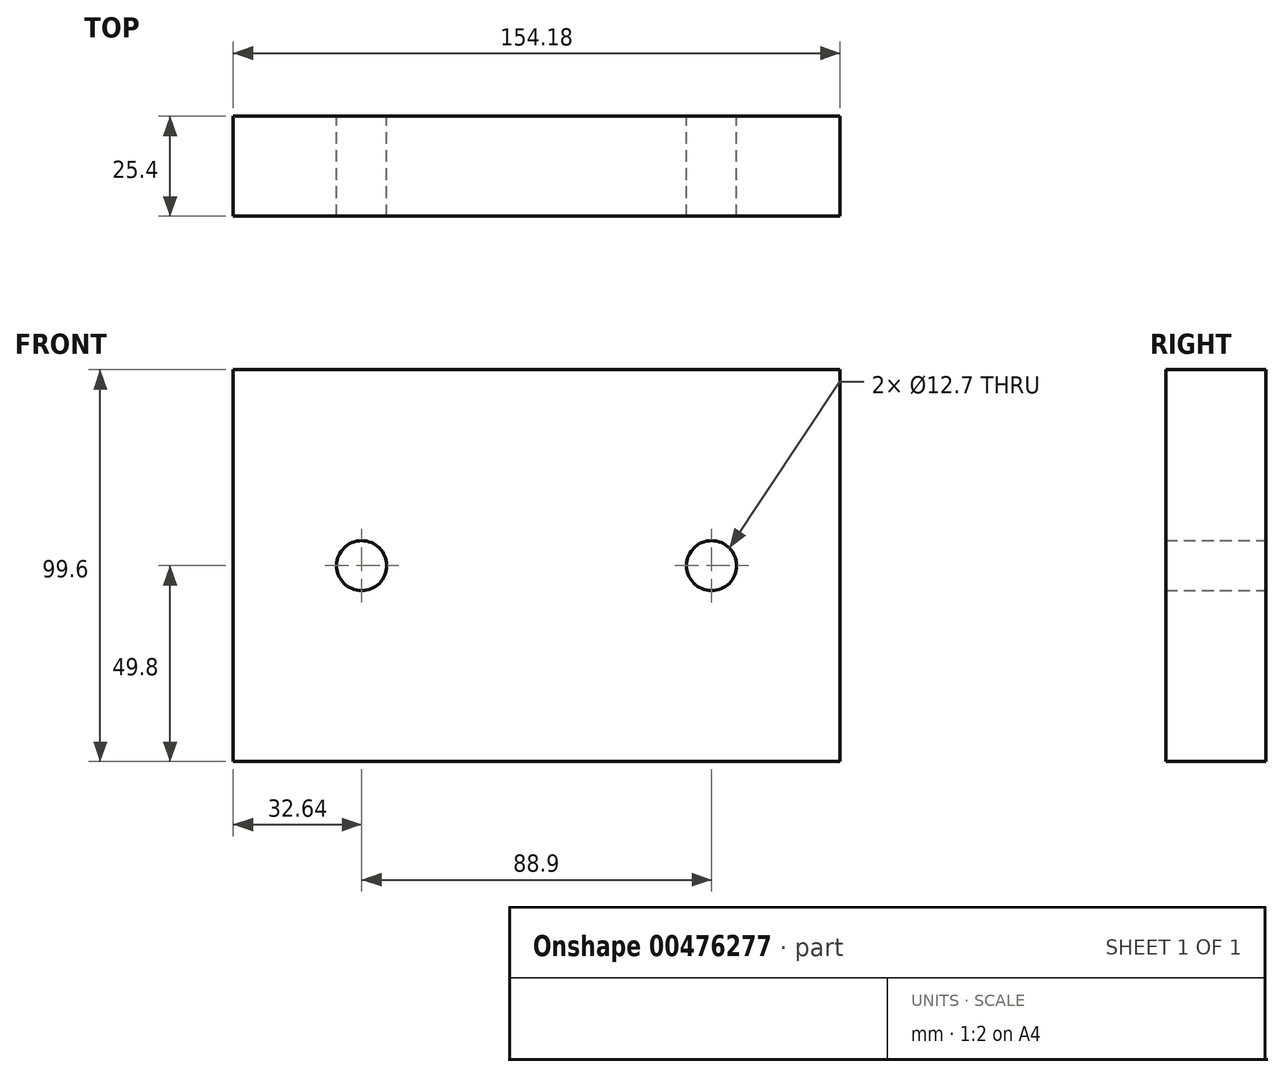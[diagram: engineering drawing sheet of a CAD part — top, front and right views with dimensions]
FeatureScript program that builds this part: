
annotation { "Feature Type Name" : "Feature", "Feature Type Description" : "" }
export const myFeature = defineFeature(function(context is Context, id is Id, definition is map)
    precondition{}
    {
        {
            var Q0;
            Q0=qCreatedBy(makeId("Front.planeOp"),FACE);
            var sketch = newSketch(context, id + "F0", { "sketchPlane" : qUnion([Q0])});
            skLineSegment(sketch, "E0.bottom", {"start": v(-77.09, 49.8) * mm, "end": v(77.09, 49.8) * mm});
            skLineSegment(sketch, "E0.top", {"start": v(-77.09, -49.8) * mm, "end": v(77.09, -49.8) * mm});
            skLineSegment(sketch, "E0.left", {"start": v(-77.09, 49.8) * mm, "end": v(-77.09, -49.8) * mm});
            skLineSegment(sketch, "E0.right", {"start": v(77.09, 49.8) * mm, "end": v(77.09, -49.8) * mm});
            skPoint(sketch, "E0.middle", {"position": v(0, 0) * mm});
            skCircle(sketch, "E1", {"center": v(-44.45, 0) * mm, "radius": 6.35 * mm});
            skCircle(sketch, "E2", {"center": v(44.45, 0) * mm, "radius": 6.35 * mm});
            skCircle(sketch, "E3", {"center": v(-44.45, 0) * mm, "radius": 50.8 * mm, "construction": true});
            skCircle(sketch, "E4", {"center": v(-44.45, 0) * mm, "radius": 63.5 * mm, "construction": true});
            skCircle(sketch, "E5", {"center": v(44.45, 0) * mm, "radius": 25.4 * mm, "construction": true});
            skCircle(sketch, "E6", {"center": v(44.45, 0) * mm, "radius": 38.1 * mm, "construction": true});
            skSolve(sketch);
        }
        {
            var Q0;
            Q0 = qSketchRegion(id + "F0", true);
            extrude(context, id + "F1", {"entities" : qUnion([Q0]), "depth" : 25.4 * mm, "offsetDistance" : 25.4 * mm});
        }
        {
            var Q0;
            Q0=makeQuery(id+"F0.imprint","IMPRINT",FACE,{"disambiguationData":[TD([[makeQuery(id+"F0.imprint","IMPRINT",EDGE,{"derivedFrom":sQuery(id+"F0.wireOp",EDGE,"E1")}),1.0]])]});
            extrude(context, id + "F2", {"entities" : qUnion([Q0]), "depth" : 25.4 * mm, "offsetDistance" : 25.4 * mm});
        }
    });
